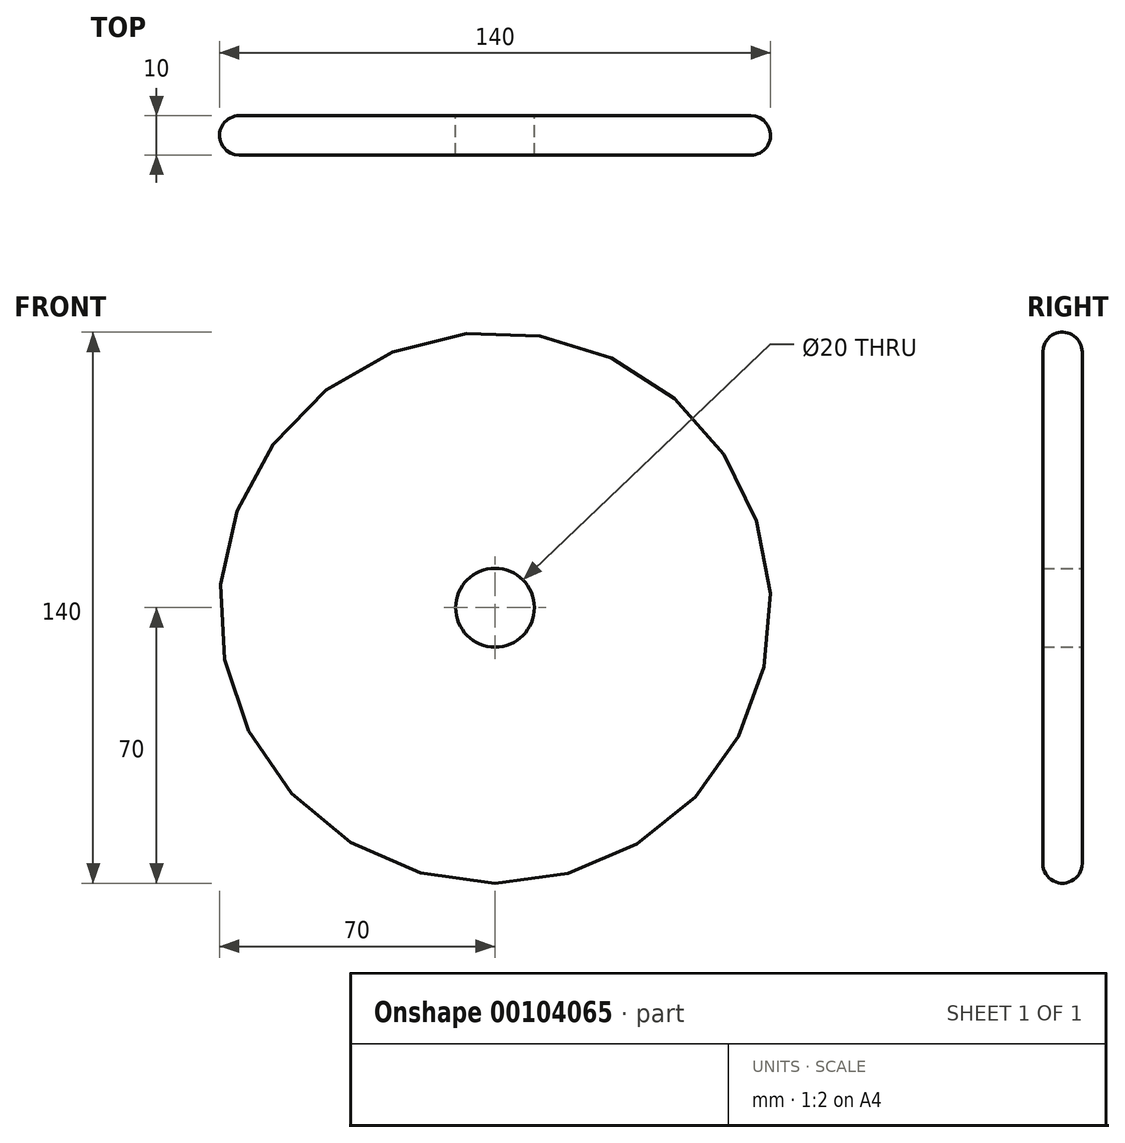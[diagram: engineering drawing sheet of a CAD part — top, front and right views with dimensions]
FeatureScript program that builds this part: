
annotation { "Feature Type Name" : "Feature", "Feature Type Description" : "" }
export const myFeature = defineFeature(function(context is Context, id is Id, definition is map)
    precondition{}
    {
        {
            var Q0;
            Q0=qCreatedBy(makeId("Front.planeOp"),FACE);
            var sketch = newSketch(context, id + "F0", { "sketchPlane" : qUnion([Q0])});
            skCircle(sketch, "E0", {"center": v(0, 0) * mm, "radius": 70 * mm});
            skCircle(sketch, "E1", {"center": v(0, 0) * mm, "radius": 10 * mm});
            skLineSegment(sketch, "E2.bottom", {"start": v(0, 70) * mm, "end": v(0, 70) * mm});
            skLineSegment(sketch, "E2.top", {"start": v(0, 0) * mm, "end": v(0, 0) * mm});
            skLineSegment(sketch, "E2.left", {"start": v(0, 70) * mm, "end": v(0, 0) * mm});
            skLineSegment(sketch, "E2.right", {"start": v(0, 70) * mm, "end": v(0, 0) * mm});
            skPoint(sketch, "E2.middle", {"position": v(0, 35) * mm});
            skSolve(sketch);
        }
        {
            var Q0;
            Q0=makeQuery(id+"F0.imprint","IMPRINT",FACE,{"disambiguationData":[TD([[makeQuery(id+"F0.imprint","IMPRINT",EDGE,{"derivedFrom":sQuery(id+"F0.wireOp",EDGE,"E0")}),1.0]])]});
            extrude(context, id + "F1", {"entities" : qUnion([Q0]), "depth" : 10 * mm});
        }
        {
            var Q0;
            Q0=makeQuery(id+"F1.opExtrude","CAP_EDGE",EDGE,{"disambiguationData":[OSD([sQuery(id+"F0.wireOp",EDGE,"E0")])],"isStart":false});
            var Q1;
            Q1=makeQuery(id+"F1.opExtrude","CAP_EDGE",EDGE,{"disambiguationData":[OSD([sQuery(id+"F0.wireOp",EDGE,"E0")])],"isStart":true});
            fillet(context, id + "F2", {"entities" : qUnion([Q0, Q1]), "radius" : 5 * mm, "tangentPropagation" : true, "allowEdgeOverflow" : false});
        }
    });
